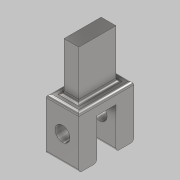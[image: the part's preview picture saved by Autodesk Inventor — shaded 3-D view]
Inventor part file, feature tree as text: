
AUTODESK INVENTOR PART (.ipt)
format: ipt  version: 2021 (Build 250183000, 183)  size: 150,016 bytes
history: native  units: mm
features: sketch x4, extrude x3, fillet x1, hole x1
ambient origin geometry x8: Origin, YZ Plane, XZ Plane, XY Plane, X Axis, Y Axis, Z Axis, Center Point
bodies: Solid1 (feature_tree)
feature tree (9):
  extrude  "sandwich_plate"  Depth=32.5mm
  extrude  "clamp_length"  Depth=12.5mm
  extrude  "slot"  Depth=35.0mm TaperAngle=0.0deg
  fillet  "Fillet1"  Radius=6.0mm
  hole  "Hole1"  [1 undecoded]
  sketch  "Sketch1"  dims[d0=25.0mm d1=32.5mm]
  sketch  "Sketch2"  dims[d2=16.25mm d3=12.5mm]
  sketch  "Sketch3"  dims[d4=10.0mm d5=0.0mm d7=35.0mm d8=0.0mm d9=6.0mm]
  sketch  "Sketch4"  dims[d10=6.0mm d11=6.0mm d12=6.0mm d14=7.5mm d15=12.0mm d16=12.0mm d17=0.0mm d18=0.0mm d19=2.0mm d20=11.0mm d21=17.5mm d22=10.0mm d23=6.0mm d24=4.0mm d25=2.0mm d26=90.0deg d27=8.0mm d28=20.594885mm d6=0.5mm]
note: 1 required parameter value undecoded (feature->parameter linkage not recoverable at this tier; creation-order binding heuristic only, values carry confidence <= 0.55)
